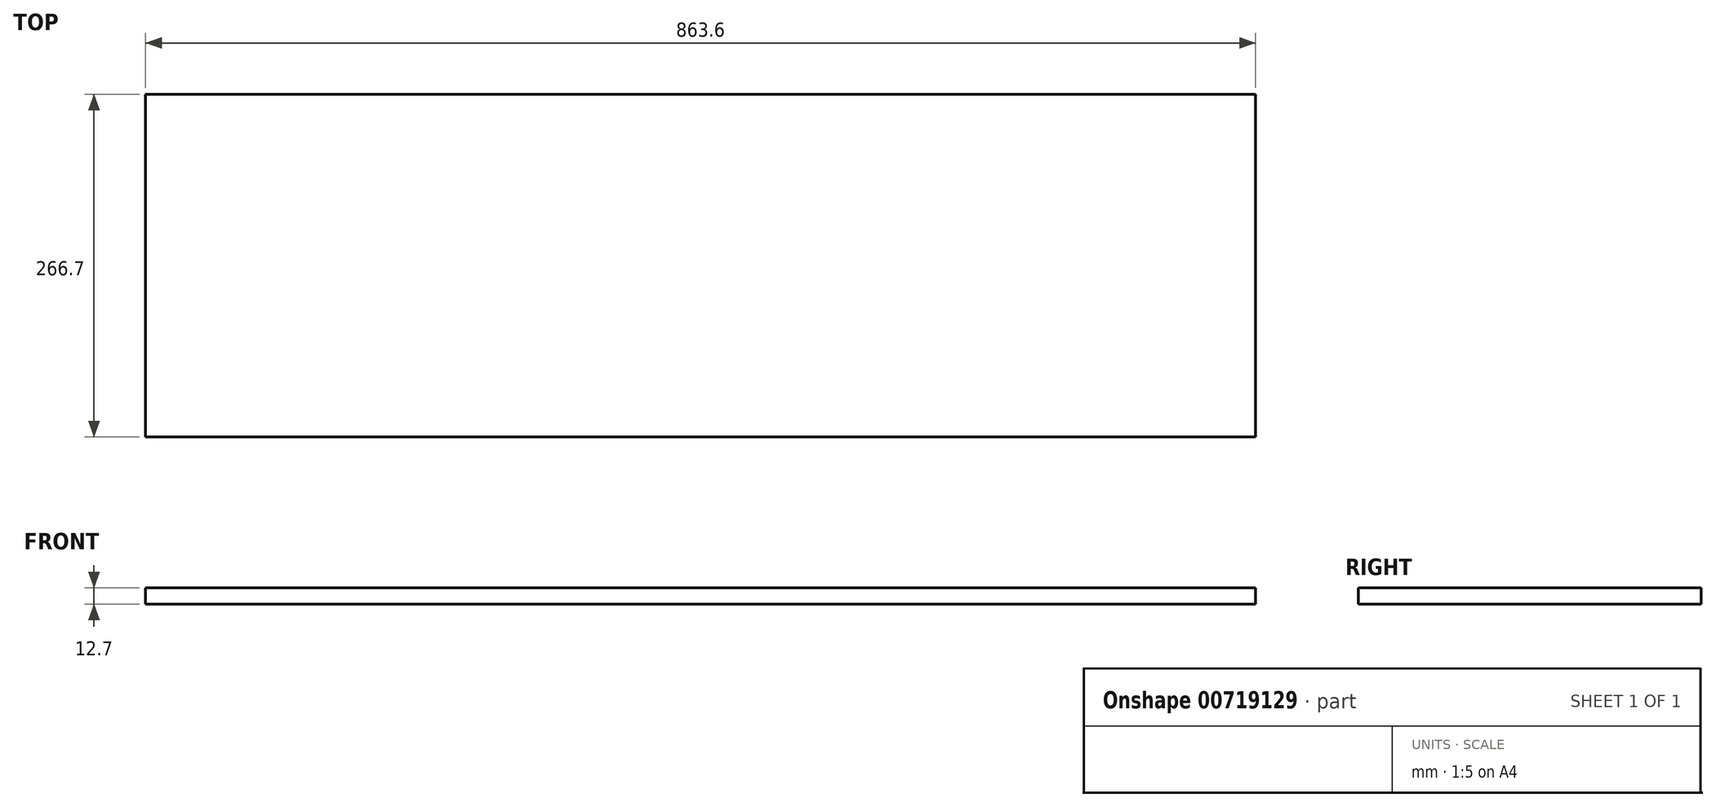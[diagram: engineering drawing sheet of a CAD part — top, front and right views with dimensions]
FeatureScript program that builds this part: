
annotation { "Feature Type Name" : "Feature", "Feature Type Description" : "" }
export const myFeature = defineFeature(function(context is Context, id is Id, definition is map)
    precondition{}
    {
        {
            var Q0;
            Q0=qCreatedBy(makeId("Top.planeOp"),FACE);
            var sketch = newSketch(context, id + "F0", { "sketchPlane" : qUnion([Q0])});
            skLineSegment(sketch, "E0.bottom", {"start": v(0, 0) * mm, "end": v(-863.6, 0) * mm});
            skLineSegment(sketch, "E0.top", {"start": v(0, 266.7) * mm, "end": v(-863.6, 266.7) * mm});
            skLineSegment(sketch, "E0.left", {"start": v(0, 0) * mm, "end": v(0, 266.7) * mm});
            skLineSegment(sketch, "E0.right", {"start": v(-863.6, 0) * mm, "end": v(-863.6, 266.7) * mm});
            skSolve(sketch);
        }
        {
            var Q0;
            Q0=makeQuery(id+"F0.imprint","IMPRINT",FACE,{"disambiguationData":[TD([[makeQuery(id+"F0.imprint","IMPRINT",EDGE,{"derivedFrom":sQuery(id+"F0.wireOp",EDGE,"E0.bottom")}),-1.0]])]});
            extrude(context, id + "F1", {"entities" : qUnion([Q0]), "depth" : 12.7 * mm, "offsetDistance" : 25.4 * mm});
        }
    });
